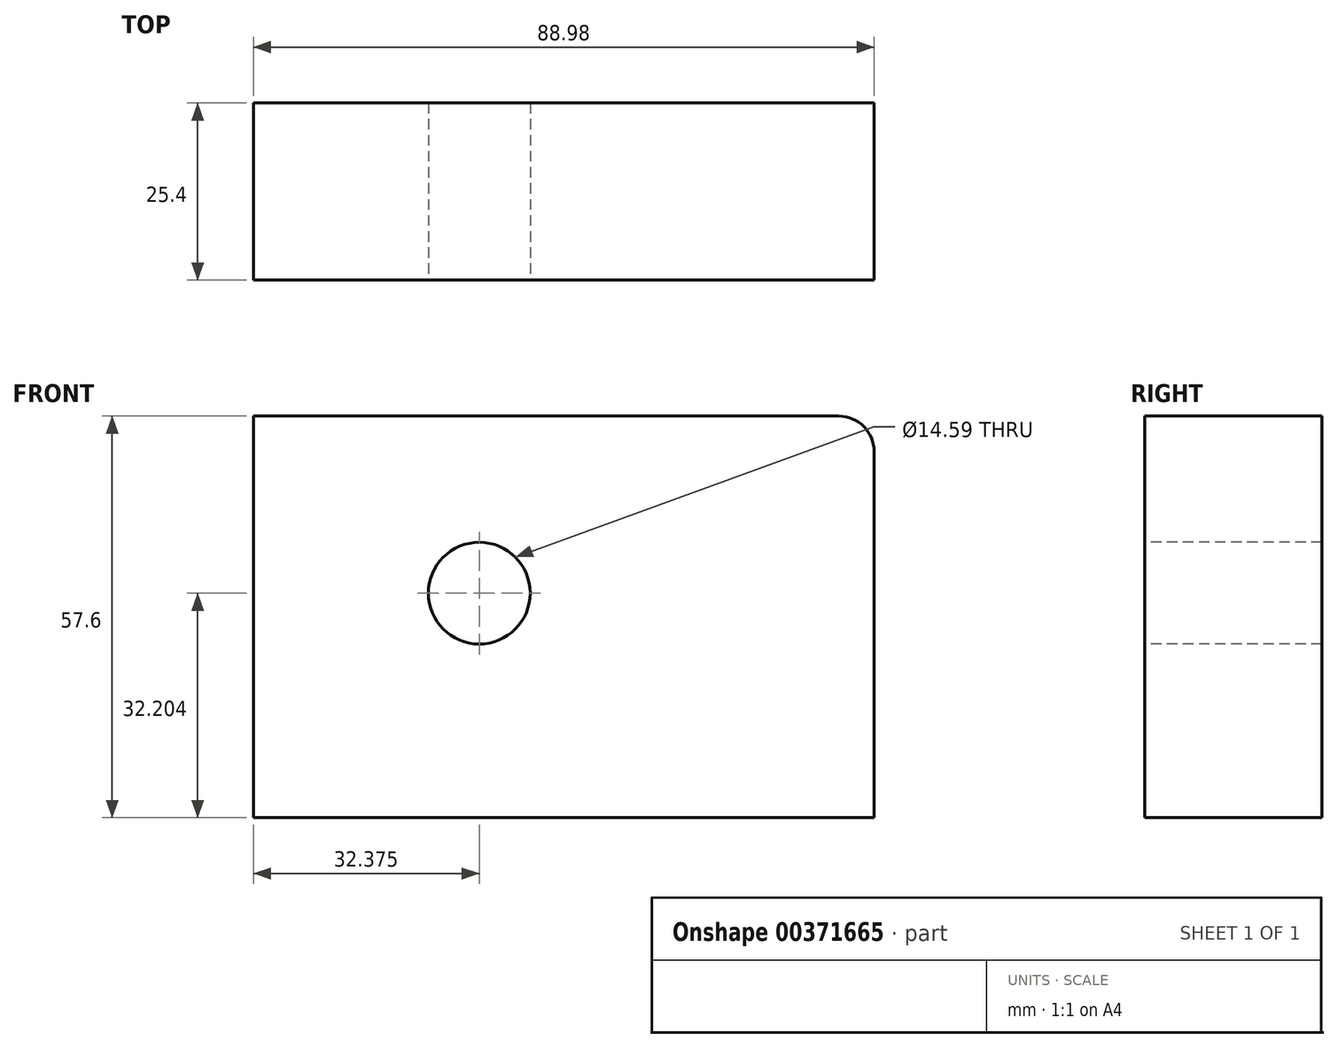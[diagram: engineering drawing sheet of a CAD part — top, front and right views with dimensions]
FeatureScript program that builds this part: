
annotation { "Feature Type Name" : "Feature", "Feature Type Description" : "" }
export const myFeature = defineFeature(function(context is Context, id is Id, definition is map)
    precondition{}
    {
        {
            var Q0;
            Q0=qCreatedBy(makeId("Front.planeOp"),FACE);
            var sketch = newSketch(context, id + "F0", { "sketchPlane" : qUnion([Q0])});
            skLineSegment(sketch, "E0.bottom", {"start": v(44.49, 28.8) * mm, "end": v(-44.49, 28.8) * mm});
            skLineSegment(sketch, "E0.top", {"start": v(44.49, -28.8) * mm, "end": v(-44.49, -28.8) * mm});
            skLineSegment(sketch, "E0.left", {"start": v(44.49, 28.8) * mm, "end": v(44.49, -28.8) * mm});
            skLineSegment(sketch, "E0.right", {"start": v(-44.49, 28.8) * mm, "end": v(-44.49, -28.8) * mm});
            skPoint(sketch, "E0.middle", {"position": v(0, 0) * mm});
            skSolve(sketch);
        }
        {
            var Q0;
            Q0 = qSketchRegion(id + "F0", true);
            extrude(context, id + "F1", {"entities" : qUnion([Q0]), "endBound" : BoundingType.SYMMETRIC, "depth" : 25.4 * mm});
        }
        {
            var Q0;
            Q0=makeQuery(id+"F1.opExtrude","CAP_FACE",FACE,{"disambiguationData":[OSD([sQuery(id+"F0.wireOp",EDGE,"E0.bottom"),sQuery(id+"F0.wireOp",EDGE,"E0.top"),sQuery(id+"F0.wireOp",EDGE,"E0.left"),sQuery(id+"F0.wireOp",EDGE,"E0.right")])],"isStart":false});
            var sketch = newSketch(context, id + "F2", { "sketchPlane" : qUnion([Q0])});
            skLineSegment(sketch, "E1", {"start": v(-34.45, 28.8) * mm, "end": v(-34.45, 3.4) * mm, "construction": true});
            skLineSegment(sketch, "E2", {"start": v(-34.45, 3.4) * mm, "end": v(-12.11, 3.4) * mm, "construction": true});
            skCircle(sketch, "E3", {"center": v(-12.11, 3.4) * mm, "radius": 7.3 * mm});
            skSolve(sketch);
        }
        {
            var Q0;
            Q0 = qSketchRegion(id + "F2", true);
            extrude(context, id + "F3", {"entities" : qUnion([Q0]), "operationType" : NewBodyOperationType.REMOVE, "endBound" : BoundingType.UP_TO_NEXT, "oppositeDirection" : true, "depth" : 25.4 * mm});
        }
        {
            var Q0;
            Q0=makeQuery(id+"F1.opExtrude","SWEPT_EDGE",EDGE,{"disambiguationData":[OSD([sQuery(id+"F0.wireOp",EDGE,"E0.bottom"),sQuery(id+"F0.wireOp",EDGE,"E0.left")])]});
            fillet(context, id + "F4", {"entities" : qUnion([Q0]), "radius" : 5.08 * mm, "tangentPropagation" : true, "allowEdgeOverflow" : false});
        }
    });
